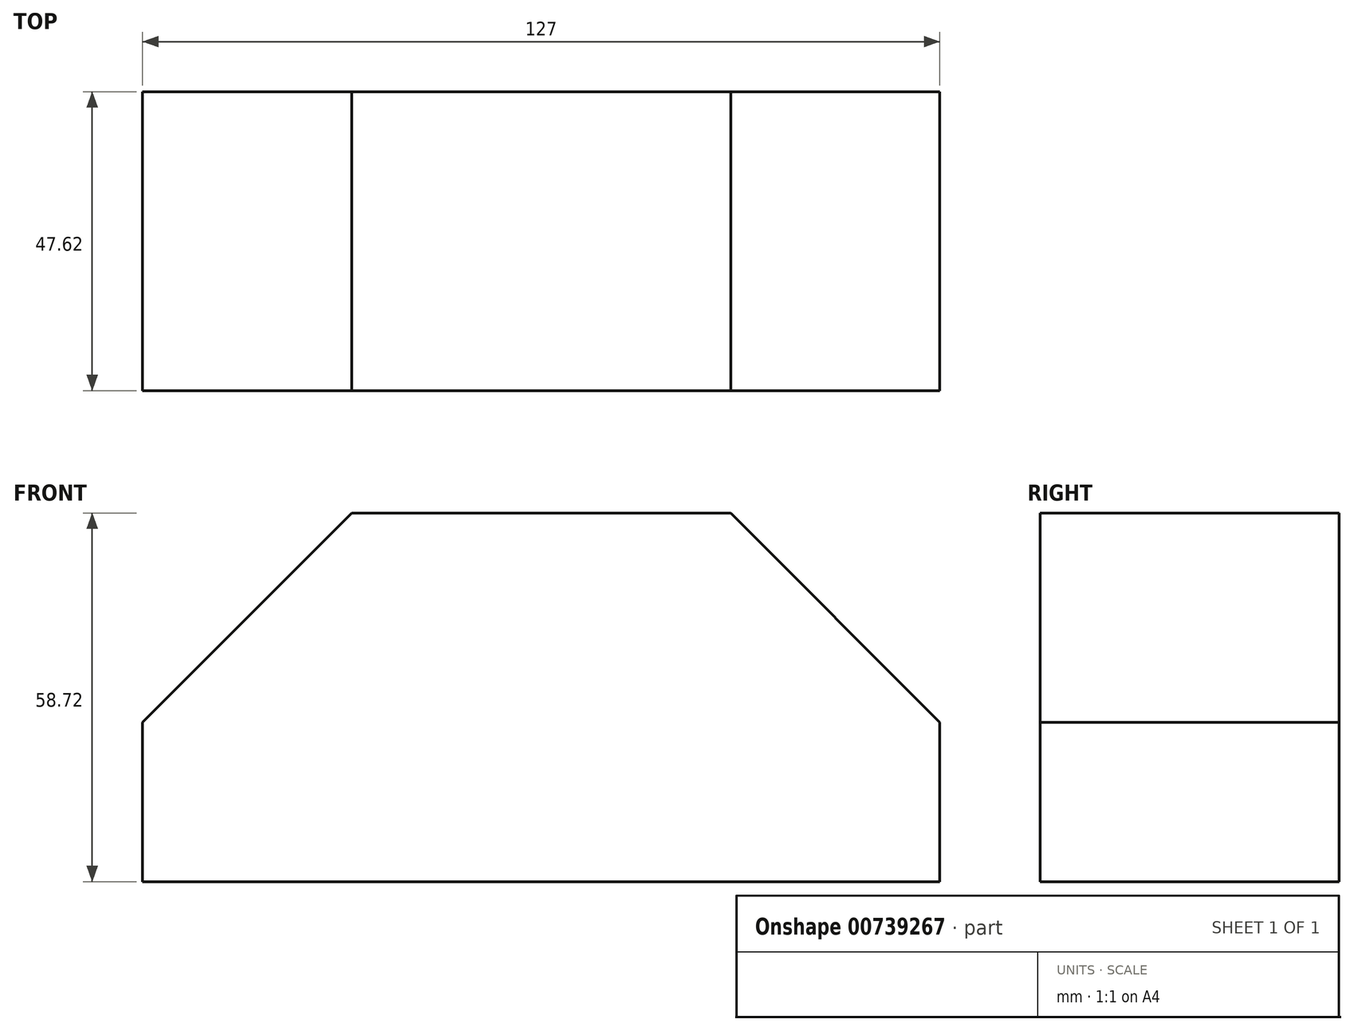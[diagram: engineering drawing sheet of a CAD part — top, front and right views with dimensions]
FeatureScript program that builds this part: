
annotation { "Feature Type Name" : "Feature", "Feature Type Description" : "" }
export const myFeature = defineFeature(function(context is Context, id is Id, definition is map)
    precondition{}
    {
        {
            var Q0;
            Q0=qCreatedBy(makeId("Front.planeOp"),FACE);
            var sketch = newSketch(context, id + "F0", { "sketchPlane" : qUnion([Q0])});
            skLineSegment(sketch, "E0", {"start": v(0, 0) * mm, "end": v(127, 0) * mm});
            skLineSegment(sketch, "E1", {"start": v(93.68, 58.72) * mm, "end": v(127, 25.4) * mm});
            skLineSegment(sketch, "E2", {"start": v(0, 25.4) * mm, "end": v(33.32, 58.72) * mm});
            skLineSegment(sketch, "E3", {"start": v(0, 0) * mm, "end": v(0, 25.4) * mm});
            skLineSegment(sketch, "E4", {"start": v(33.32, 58.72) * mm, "end": v(93.68, 58.72) * mm});
            skLineSegment(sketch, "E5", {"start": v(127, 25.4) * mm, "end": v(127, 0) * mm});
            skSolve(sketch);
        }
        {
            var Q0;
            Q0=makeQuery(id+"F0.imprint","IMPRINT",FACE,{"disambiguationData":[TD([[makeQuery(id+"F0.imprint","IMPRINT",EDGE,{"derivedFrom":sQuery(id+"F0.wireOp",EDGE,"E0")}),1.0]])]});
            extrude(context, id + "F1", {"entities" : qUnion([Q0]), "depth" : 47.62 * mm, "offsetDistance" : 25.4 * mm});
        }
    });
